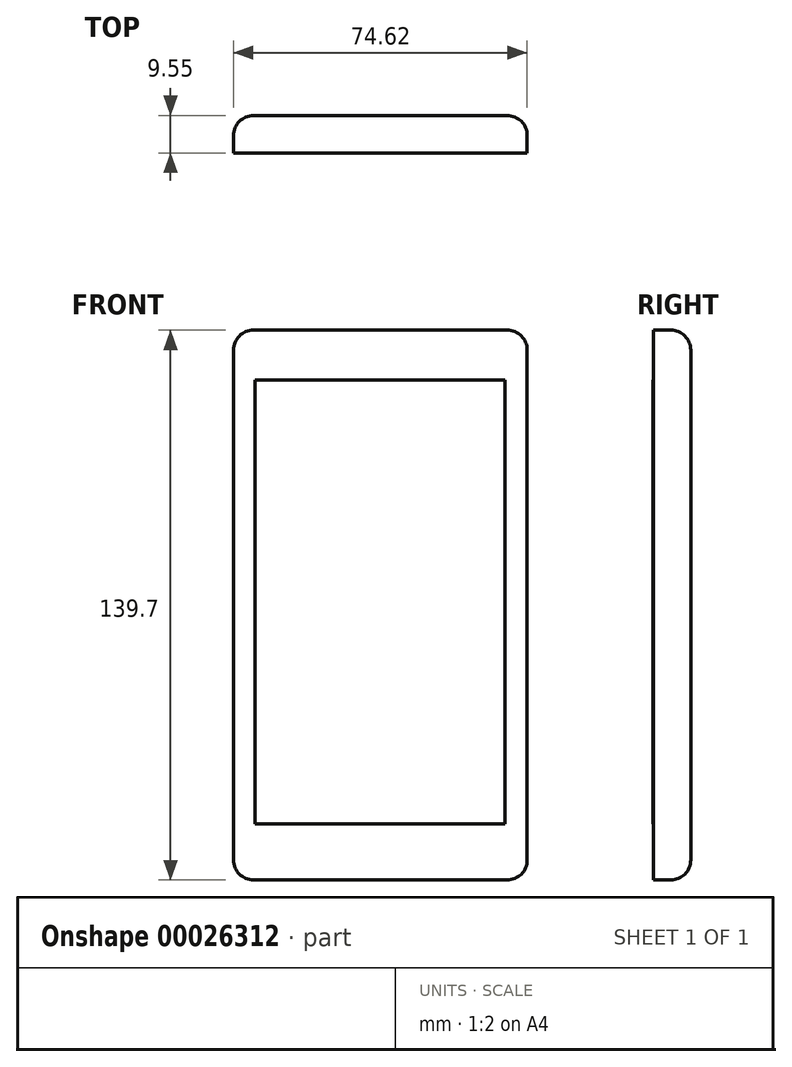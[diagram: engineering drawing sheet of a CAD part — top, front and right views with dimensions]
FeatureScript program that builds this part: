
annotation { "Feature Type Name" : "Feature", "Feature Type Description" : "" }
export const myFeature = defineFeature(function(context is Context, id is Id, definition is map)
    precondition{}
    {
        {
            var Q0;
            Q0=qCreatedBy(makeId("Front.planeOp"),FACE);
            var sketch = newSketch(context, id + "F0", { "sketchPlane" : qUnion([Q0])});
            skLineSegment(sketch, "E0.bottom", {"start": v(-15.1, 63.78) * mm, "end": v(59.52, 63.78) * mm});
            skLineSegment(sketch, "E0.top", {"start": v(-15.1, -75.92) * mm, "end": v(59.52, -75.92) * mm});
            skLineSegment(sketch, "E0.left", {"start": v(-15.1, 63.78) * mm, "end": v(-15.1, -75.92) * mm});
            skLineSegment(sketch, "E0.right", {"start": v(59.52, 63.78) * mm, "end": v(59.52, -75.92) * mm});
            skSolve(sketch);
        }
        {
            var Q0;
            Q0 = qSketchRegion(id + "F0", true);
            extrude(context, id + "F1", {"entities" : qUnion([Q0]), "depth" : 9.52 * mm});
        }
        {
            var Q0;
            Q0=makeQuery(id+"F1.opExtrude","SWEPT_EDGE",EDGE,{"disambiguationData":[OSD([sQuery(id+"F0.wireOp",EDGE,"E0.bottom"),sQuery(id+"F0.wireOp",EDGE,"E0.right")])]});
            var Q1;
            Q1=makeQuery(id+"F1.opExtrude","SWEPT_EDGE",EDGE,{"disambiguationData":[OSD([sQuery(id+"F0.wireOp",EDGE,"E0.top"),sQuery(id+"F0.wireOp",EDGE,"E0.right")])]});
            var Q2;
            Q2=makeQuery(id+"F1.opExtrude","SWEPT_EDGE",EDGE,{"disambiguationData":[OSD([sQuery(id+"F0.wireOp",EDGE,"E0.top"),sQuery(id+"F0.wireOp",EDGE,"E0.left")])]});
            var Q3;
            Q3=makeQuery(id+"F1.opExtrude","SWEPT_EDGE",EDGE,{"disambiguationData":[OSD([sQuery(id+"F0.wireOp",EDGE,"E0.bottom"),sQuery(id+"F0.wireOp",EDGE,"E0.left")])]});
            var Q4;
            Q4=makeQuery(id+"F1.opExtrude","CAP_EDGE",EDGE,{"disambiguationData":[OSD([sQuery(id+"F0.wireOp",EDGE,"E0.bottom")])],"isStart":true});
            var Q5;
            Q5=makeQuery(id+"F1.opExtrude","CAP_EDGE",EDGE,{"disambiguationData":[OSD([sQuery(id+"F0.wireOp",EDGE,"E0.right")])],"isStart":true});
            var Q6;
            Q6=makeQuery(id+"F1.opExtrude","CAP_EDGE",EDGE,{"disambiguationData":[OSD([sQuery(id+"F0.wireOp",EDGE,"E0.top")])],"isStart":true});
            var Q7;
            Q7=makeQuery(id+"F1.opExtrude","CAP_EDGE",EDGE,{"disambiguationData":[OSD([sQuery(id+"F0.wireOp",EDGE,"E0.left")])],"isStart":true});
            fillet(context, id + "F2", {"entities" : qUnion([Q0, Q1, Q2, Q3, Q4, Q5, Q6, Q7]), "radius" : 5.08 * mm, "tangentPropagation" : true, "allowEdgeOverflow" : false});
        }
        {
            var Q0;
            Q0=makeQuery(id+"F1.opExtrude","CAP_FACE",FACE,{"disambiguationData":[OSD([sQuery(id+"F0.wireOp",EDGE,"E0.bottom"),sQuery(id+"F0.wireOp",EDGE,"E0.top"),sQuery(id+"F0.wireOp",EDGE,"E0.left"),sQuery(id+"F0.wireOp",EDGE,"E0.right")])],"isStart":false});
            var sketch = newSketch(context, id + "F3", { "sketchPlane" : qUnion([Q0])});
            skLineSegment(sketch, "E1.bottom", {"start": v(53.92, 51.06) * mm, "end": v(-9.58, 51.06) * mm});
            skLineSegment(sketch, "E1.top", {"start": v(53.92, -61.65) * mm, "end": v(-9.58, -61.65) * mm});
            skLineSegment(sketch, "E1.left", {"start": v(53.92, 51.06) * mm, "end": v(53.92, -61.65) * mm});
            skLineSegment(sketch, "E1.right", {"start": v(-9.58, 51.06) * mm, "end": v(-9.58, -61.65) * mm});
            skSolve(sketch);
        }
        {
            var Q0;
            Q0 = qSketchRegion(id + "F3", true);
            extrude(context, id + "F4", {"entities" : qUnion([Q0]), "depth" : 0.03 * mm});
        }
    });
